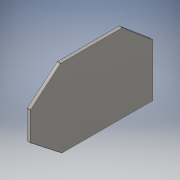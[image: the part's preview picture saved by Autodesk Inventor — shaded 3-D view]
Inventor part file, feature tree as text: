
AUTODESK INVENTOR PART (.ipt)
format: ipt  version: 2016 (Build 200138000, 138)  size: 232,448 bytes
history: native  units: mm
features: sheet_metal_op x7, other x4, sketch x3
ambient origin geometry x8: Origin, YZ Plane, XZ Plane, XY Plane, X Axis, Y Axis, Z Axis, Center Point
bodies: Solid1 (feature_tree)
feature tree (14):
  sheet_metal_op  "Face1"
  sheet_metal_op  "Flange1"
  sheet_metal_op  "Flange2"
  sketch  "Sketch1"  dims[d0=472.0mm]
  other  "Plate1"
  sketch  "Sketch2"  dims[d1=350.0mm]
  other  "Plate2"
  sheet_metal_op  "Bend1"
  sheet_metal_op  "Corner1"
  sketch  "Sketch3"  dims[d2=22.68928mm d3=550.0mm d4=350.0mm d5=24.43461mm d6=252.0mm d8=22.340214mm d9=1.6mm d10=1.6mm d11=0.8mm d12=3.2mm d13=1.6mm d14=30.0mm d15=90.0deg d16=1.6mm d17=6.4mm d18=1.6mm d19=1.6mm d20=1.6mm d21=0.8mm d22=3.2mm d23=1.6mm d24=30.0mm d25=90.0deg d26=1.6mm d27=6.4mm d28=1.6mm d29=1.6mm]
  other  "Plate3"
  sheet_metal_op  "Bend2"
  sheet_metal_op  "Corner2"
  other  "Definition1"
